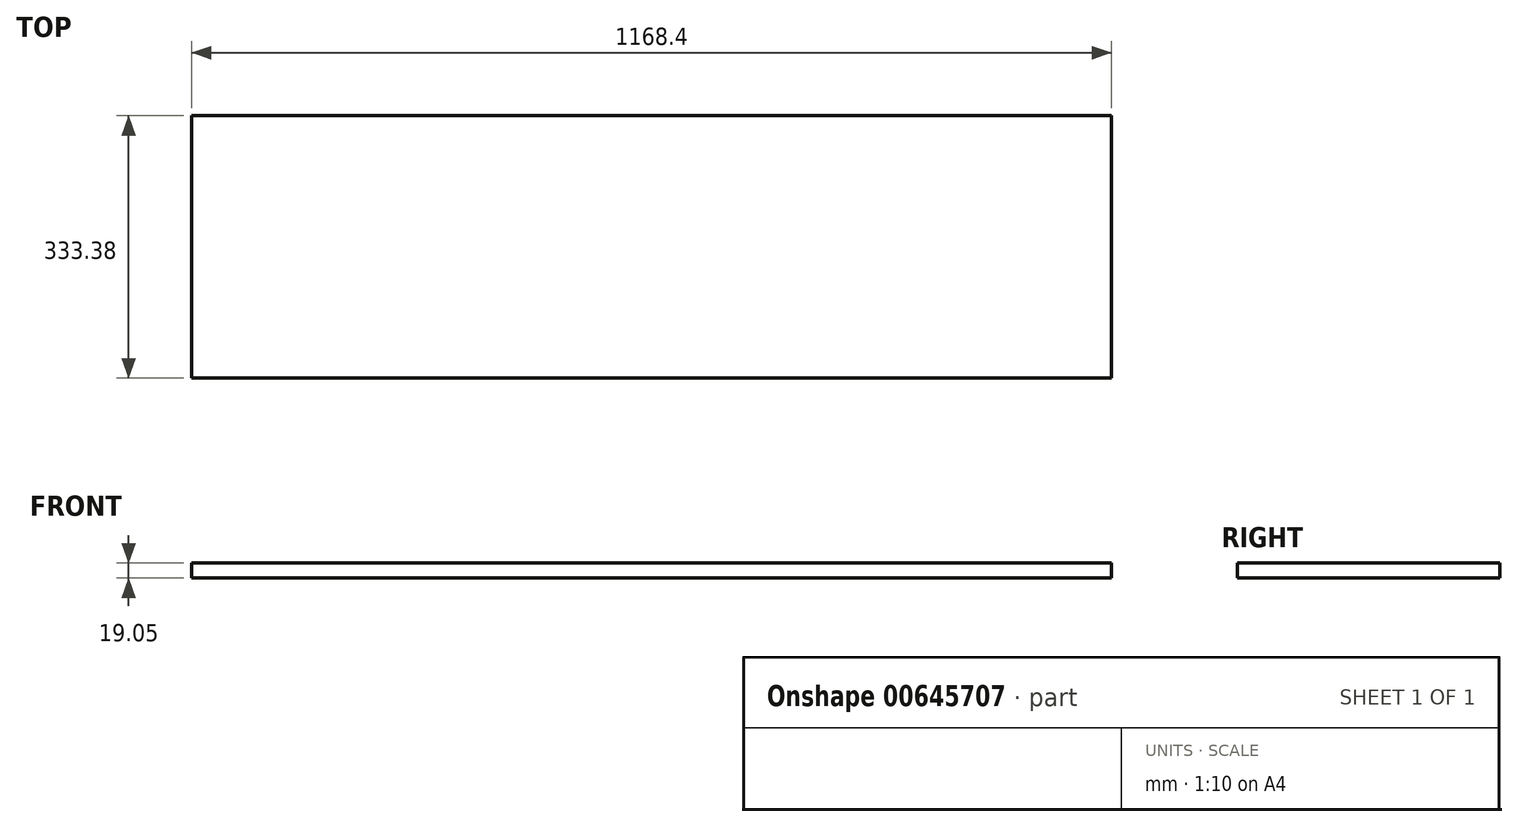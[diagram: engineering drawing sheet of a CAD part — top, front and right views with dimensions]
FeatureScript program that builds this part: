
annotation { "Feature Type Name" : "Feature", "Feature Type Description" : "" }
export const myFeature = defineFeature(function(context is Context, id is Id, definition is map)
    precondition{}
    {
        {
            var Q0;
            Q0=qCreatedBy(makeId("Top.planeOp"),FACE);
            var sketch = newSketch(context, id + "F0", { "sketchPlane" : qUnion([Q0])});
            skLineSegment(sketch, "E0.bottom", {"start": v(-584.2, 166.69) * mm, "end": v(584.2, 166.69) * mm});
            skLineSegment(sketch, "E0.top", {"start": v(-584.2, -166.69) * mm, "end": v(584.2, -166.69) * mm});
            skLineSegment(sketch, "E0.left", {"start": v(-584.2, 166.69) * mm, "end": v(-584.2, -166.69) * mm});
            skLineSegment(sketch, "E0.right", {"start": v(584.2, 166.69) * mm, "end": v(584.2, -166.69) * mm});
            skPoint(sketch, "E0.middle", {"position": v(0, 0) * mm});
            skSolve(sketch);
        }
        {
            var Q0;
            Q0=makeQuery(id+"F0.imprint","IMPRINT",FACE,{"disambiguationData":[TD([[makeQuery(id+"F0.imprint","IMPRINT",EDGE,{"derivedFrom":sQuery(id+"F0.wireOp",EDGE,"E0.bottom")}),-1.0]])]});
            extrude(context, id + "F1", {"entities" : qUnion([Q0]), "depth" : 19.05 * mm, "offsetDistance" : 25.4 * mm});
        }
    });
